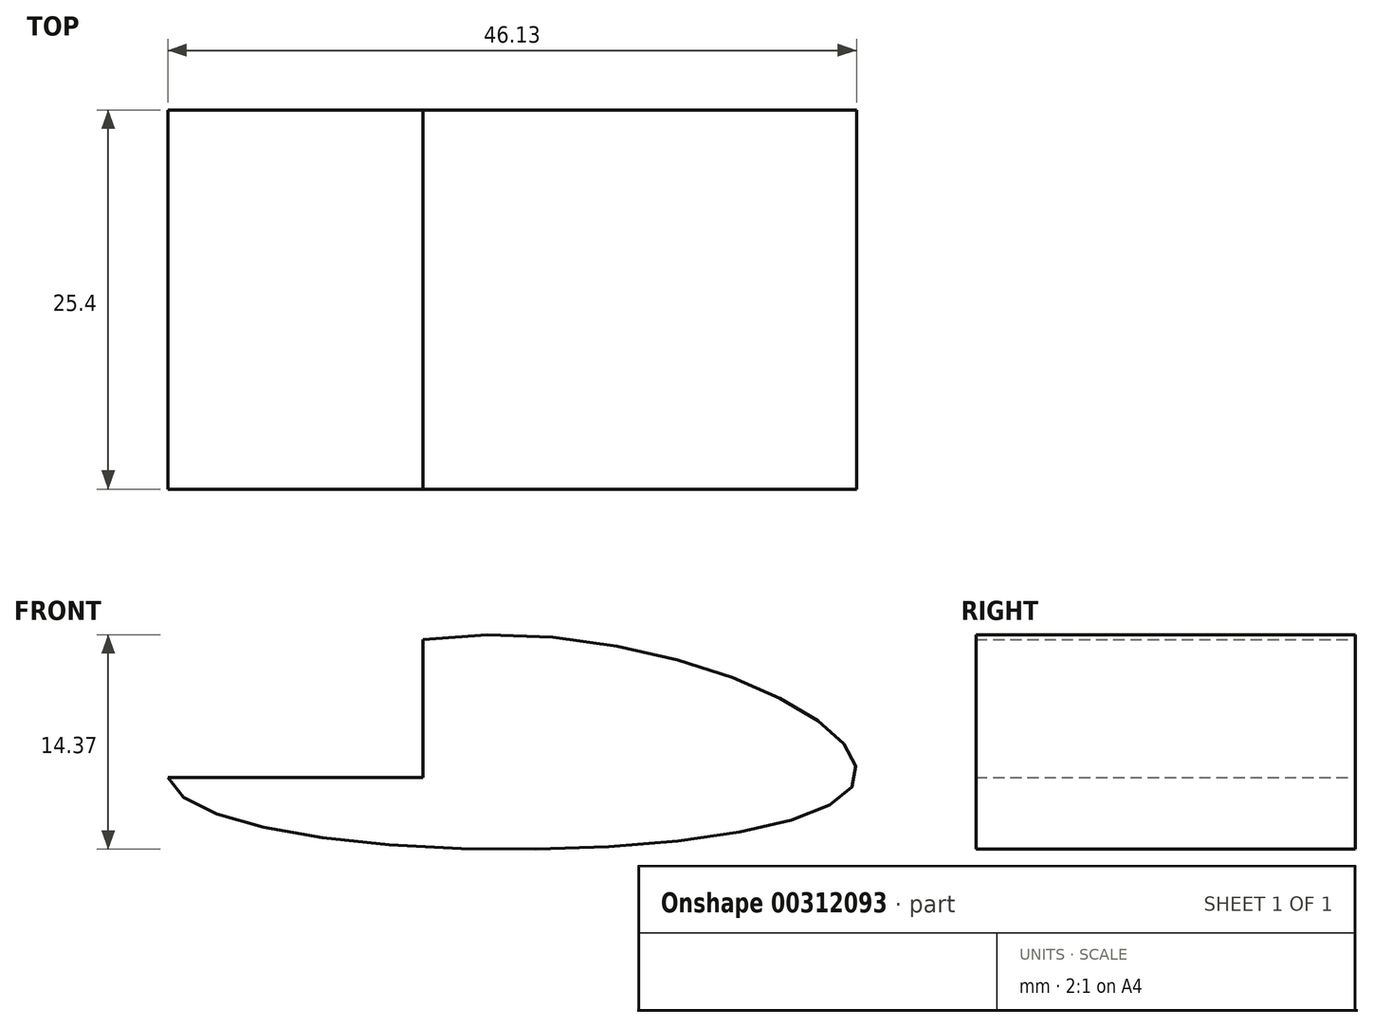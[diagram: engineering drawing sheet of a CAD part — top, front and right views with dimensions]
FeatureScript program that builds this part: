
annotation { "Feature Type Name" : "Feature", "Feature Type Description" : "" }
export const myFeature = defineFeature(function(context is Context, id is Id, definition is map)
    precondition{}
    {
        {
            var Q0;
            Q0=qCreatedBy(makeId("Front.planeOp"),FACE);
            var sketch = newSketch(context, id + "F0", { "sketchPlane" : qUnion([Q0])});
            skFitSpline(sketch, "E0", {"points": [v(-20.6, 0) * mm, v(0, 10.5) * mm, v(24.38, 0) * mm, v(-20.6, 0) * mm]});
            skSolve(sketch);
        }
        {
            var Q0;
            Q0 = qSketchRegion(id + "F0", true);
            extrude(context, id + "F1", {"entities" : qUnion([Q0]), "depth" : 25.4 * mm});
        }
        {
            var Q0;
            Q0=makeQuery(id+"F1.opExtrude","CAP_FACE",FACE,{"disambiguationData":[OSD([sQuery(id+"F0.wireOp",EDGE,"E0")])],"isStart":false});
            var sketch = newSketch(context, id + "F2", { "sketchPlane" : qUnion([Q0])});
            skLineSegment(sketch, "E1.bottom", {"start": v(-24.6, 14.68) * mm, "end": v(-4.1, 14.68) * mm});
            skLineSegment(sketch, "E1.top", {"start": v(-24.6, 0.94) * mm, "end": v(-4.1, 0.94) * mm});
            skLineSegment(sketch, "E1.left", {"start": v(-24.6, 14.68) * mm, "end": v(-24.6, 0.94) * mm});
            skLineSegment(sketch, "E1.right", {"start": v(-4.1, 14.68) * mm, "end": v(-4.1, 0.94) * mm});
            skSolve(sketch);
        }
        {
            var Q0;
            Q0 = qSketchRegion(id + "F2", true);
            extrude(context, id + "F3", {"entities" : qUnion([Q0]), "operationType" : NewBodyOperationType.REMOVE, "oppositeDirection" : true, "depth" : 25.4 * mm});
        }
    });
